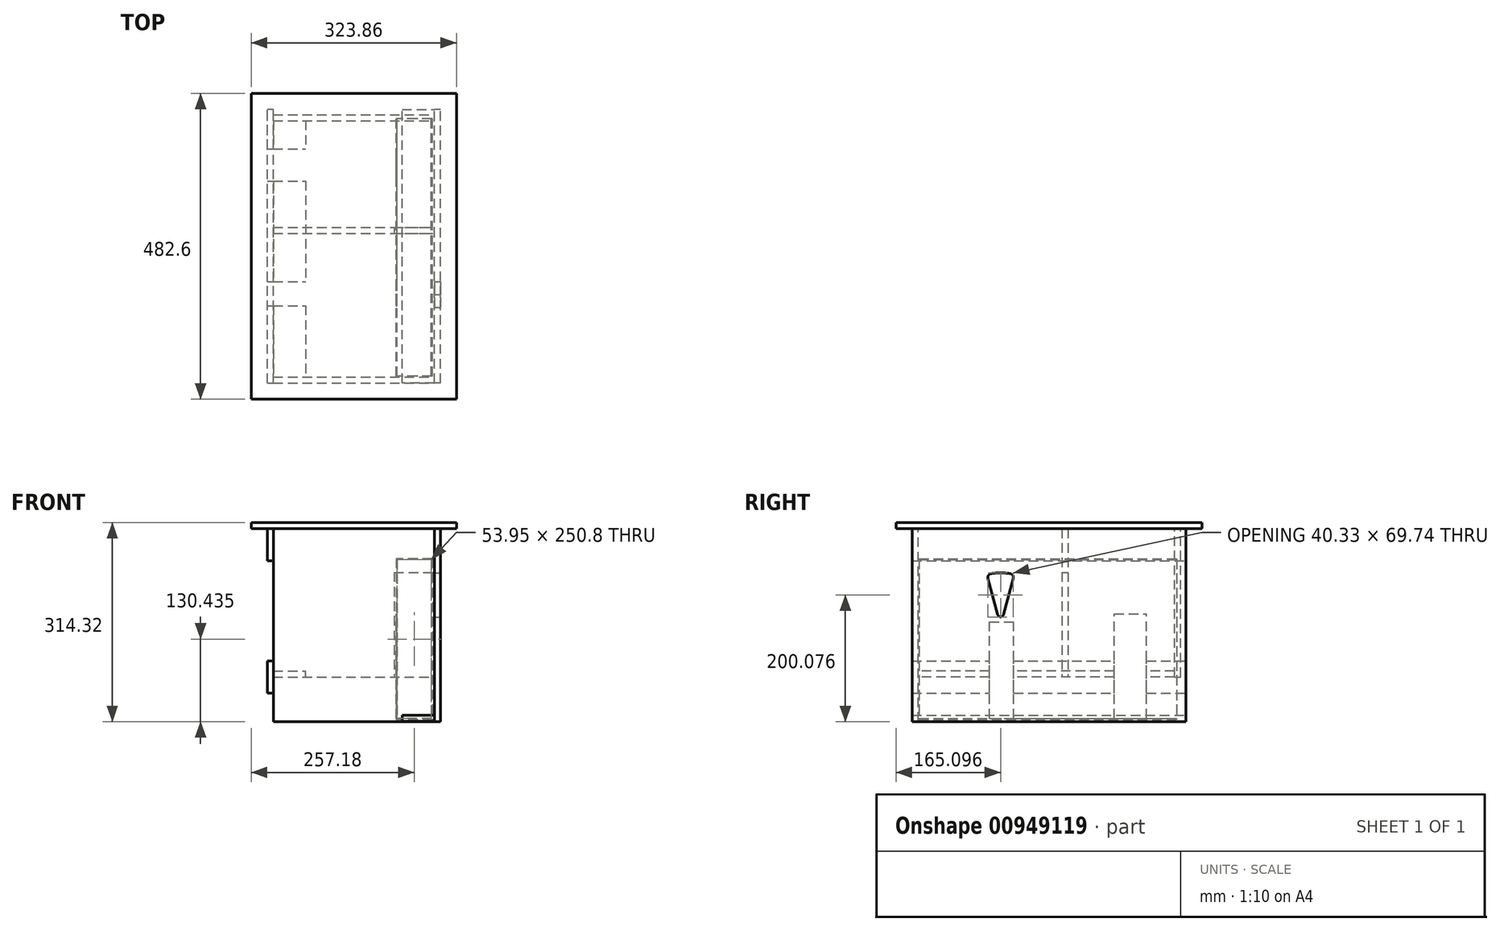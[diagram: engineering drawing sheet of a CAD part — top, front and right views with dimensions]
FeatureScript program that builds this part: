
annotation { "Feature Type Name" : "Feature", "Feature Type Description" : "" }
export const myFeature = defineFeature(function(context is Context, id is Id, definition is map)
    precondition{}
    {
        {
            var Q0;
            Q0=qCreatedBy(makeId("Right.planeOp"),FACE);
            var sketch = newSketch(context, id + "F0", { "sketchPlane" : qUnion([Q0])});
            skLineSegment(sketch, "E0", {"start": v(-148.93, -18.34) * mm, "end": v(130.45, -14.96) * mm});
            skCircle(sketch, "E1", {"center": v(-116.9, 185.56) * mm, "radius": 114.3 * mm});
            skCircle(sketch, "E2", {"center": v(85.94, 209.07) * mm, "radius": 38.1 * mm});
            skCircle(sketch, "E3", {"center": v(142.36, 82.13) * mm, "radius": 9.5 * mm});
            skCircle(sketch, "E4", {"center": v(187.36, 99.59) * mm, "radius": 9.5 * mm});
            skLineSegment(sketch, "E5", {"start": v(-180.7, 129.14) * mm, "end": v(192.06, 129.14) * mm});
            skLineSegment(sketch, "E6", {"start": v(-122.27, 219.14) * mm, "end": v(-101.44, 219.14) * mm});
            skLineSegment(sketch, "E7", {"start": v(-10.1, 98.92) * mm, "end": v(14.75, 107.65) * mm});
            skCircle(sketch, "E8", {"center": v(8.03, 88.17) * mm, "radius": 9.5 * mm});
            skSolve(sketch);
        }
        {
            var Q0;
            Q0=qCreatedBy(makeId("Top.planeOp"),FACE);
            var sketch = newSketch(context, id + "F1", { "sketchPlane" : qUnion([Q0])});
            skLineSegment(sketch, "E9.bottom", {"start": v(-42.95, 107.55) * mm, "end": v(-29.2, 107.55) * mm});
            skLineSegment(sketch, "E9.top", {"start": v(-42.95, 62.2) * mm, "end": v(-29.2, 62.2) * mm});
            skLineSegment(sketch, "E9.left", {"start": v(-42.95, 107.55) * mm, "end": v(-42.95, 62.2) * mm});
            skLineSegment(sketch, "E9.right", {"start": v(-29.2, 107.55) * mm, "end": v(-29.2, 62.2) * mm});
            skLineSegment(sketch, "E10.bottom", {"start": v(-48.66, -104.64) * mm, "end": v(-33.18, -104.64) * mm});
            skLineSegment(sketch, "E10.top", {"start": v(-48.66, -129.08) * mm, "end": v(-33.18, -129.08) * mm});
            skLineSegment(sketch, "E10.left", {"start": v(-48.66, -104.64) * mm, "end": v(-48.66, -129.08) * mm});
            skLineSegment(sketch, "E10.right", {"start": v(-33.18, -104.64) * mm, "end": v(-33.18, -129.08) * mm});
            skLineSegment(sketch, "E11", {"start": v(-46.2, 165.85) * mm, "end": v(-46.2, 7.96) * mm});
            skLineSegment(sketch, "E12", {"start": v(-51.91, -73.7) * mm, "end": v(-51.91, -164.92) * mm});
            skLineSegment(sketch, "E13.bottom", {"start": v(-23.4, -6.61) * mm, "end": v(16.15, -6.61) * mm});
            skLineSegment(sketch, "E13.top", {"start": v(-23.4, -228.46) * mm, "end": v(16.15, -228.46) * mm});
            skLineSegment(sketch, "E13.left", {"start": v(-23.4, -6.61) * mm, "end": v(-23.4, -228.46) * mm});
            skLineSegment(sketch, "E13.right", {"start": v(16.15, -6.61) * mm, "end": v(16.15, -228.46) * mm});
            skLineSegment(sketch, "E14.bottom", {"start": v(-11.19, 125.36) * mm, "end": v(9.67, 125.36) * mm});
            skLineSegment(sketch, "E14.top", {"start": v(-11.19, 44.4) * mm, "end": v(9.67, 44.4) * mm});
            skLineSegment(sketch, "E14.left", {"start": v(-11.19, 125.36) * mm, "end": v(-11.19, 44.4) * mm});
            skLineSegment(sketch, "E14.right", {"start": v(9.67, 125.36) * mm, "end": v(9.67, 44.4) * mm});
            skLineSegment(sketch, "E15.bottom", {"start": v(19.39, 92.98) * mm, "end": v(9.67, 92.98) * mm});
            skLineSegment(sketch, "E15.top", {"start": v(19.39, 75.97) * mm, "end": v(9.67, 75.97) * mm});
            skLineSegment(sketch, "E15.left", {"start": v(19.39, 92.98) * mm, "end": v(19.39, 75.97) * mm});
            skLineSegment(sketch, "E15.right", {"start": v(9.67, 92.98) * mm, "end": v(9.67, 75.97) * mm});
            skLineSegment(sketch, "E16", {"start": v(-21.1, 178.8) * mm, "end": v(-21.1, 106.74) * mm});
            skLineSegment(sketch, "E17.bottom", {"start": v(-26.76, 9.58) * mm, "end": v(18.58, 4.72) * mm});
            skLineSegment(sketch, "E17.top", {"start": v(-29.12, -12.45) * mm, "end": v(16.22, -17.31) * mm});
            skLineSegment(sketch, "E17.left", {"start": v(-26.76, 9.58) * mm, "end": v(-29.12, -12.45) * mm});
            skLineSegment(sketch, "E17.right", {"start": v(18.58, 4.72) * mm, "end": v(16.22, -17.31) * mm});
            skCircle(sketch, "E18", {"center": v(-117.44, -142.64) * mm, "radius": 73.87 * mm});
            skLineSegment(sketch, "E19", {"start": v(0, -116.9) * mm, "end": v(98.98, -116.9) * mm});
            skLineSegment(sketch, "E20", {"start": v(0, 85.94) * mm, "end": v(94.12, 85.94) * mm});
            skSolve(sketch);
        }
        {
            var Q0;
            Q0=qCreatedBy(makeId("Right.planeOp"),FACE);
            var sketch = newSketch(context, id + "F2", { "sketchPlane" : qUnion([Q0])});
            skLineSegment(sketch, "E21", {"start": v(-131.58, 219.14) * mm, "end": v(-90.11, 219.14) * mm});
            skLineSegment(sketch, "E22.0", {"start": v(-256.6, 58.56) * mm, "end": v(175.2, 58.56) * mm});
            skLineSegment(sketch, "E23", {"start": v(-256.6, 363.36) * mm, "end": v(175.2, 363.36) * mm});
            skLineSegment(sketch, "E24", {"start": v(175.2, 363.36) * mm, "end": v(175.2, 58.56) * mm});
            skLineSegment(sketch, "E25", {"start": v(-256.6, 363.36) * mm, "end": v(-256.6, 58.56) * mm});
            skPoint(sketch, "E26.orphan", {"position": v(-180.7, 129.14) * mm});
            skPoint(sketch, "E27.orphan", {"position": v(192.06, 129.14) * mm});
            skCircle(sketch, "E28.0", {"center": v(85.94, 209.07) * mm, "radius": 38.1 * mm, "construction": true});
            skCircle(sketch, "E29.0", {"center": v(-116.9, 185.56) * mm, "radius": 114.3 * mm, "construction": true});
            skLineSegment(sketch, "E30", {"start": v(124.04, 209.07) * mm, "end": v(175.2, 209.07) * mm, "construction": true});
            skLineSegment(sketch, "E31", {"start": v(-231.2, 185.56) * mm, "end": v(-256.6, 185.56) * mm, "construction": true});
            skLineSegment(sketch, "E32", {"start": v(-116.9, 299.86) * mm, "end": v(-116.9, 363.36) * mm, "construction": true});
            skSolve(sketch);
        }
        {
            var Q0;
            Q0 = qSketchRegion(id + "F2", true);
            extrude(context, id + "F3", {"entities" : qUnion([Q0]), "depth" : 41.27 * mm, "offsetDistance" : 25.4 * mm, "hasSecondDirection" : true, "secondDirectionOppositeDirection" : false, "secondDirectionDepth" : 31.75 * mm});
        }
        {
            var Q0;
            Q0=makeQuery(id+"F3.opExtrude","CAP_FACE",FACE,{"disambiguationData":[OSD([sQuery(id+"F2.wireOp",EDGE,"E22.0"),sQuery(id+"F2.wireOp",EDGE,"E23"),sQuery(id+"F2.wireOp",EDGE,"E24"),sQuery(id+"F2.wireOp",EDGE,"E25")])],"isStart":true});
            var sketch = newSketch(context, id + "F4", { "sketchPlane" : qUnion([Q0])});
            skLineSegment(sketch, "E33.bottom", {"start": v(10.68, 363.36) * mm, "end": v(20.2, 363.36) * mm});
            skLineSegment(sketch, "E33.top", {"start": v(10.68, 129.14) * mm, "end": v(20.2, 129.14) * mm});
            skLineSegment(sketch, "E33.left", {"start": v(10.68, 363.36) * mm, "end": v(10.68, 129.14) * mm});
            skLineSegment(sketch, "E33.right", {"start": v(20.2, 363.36) * mm, "end": v(20.2, 129.14) * mm});
            skSolve(sketch);
        }
        {
            var Q0;
            Q0 = qSketchRegion(id + "F4", true);
            extrude(context, id + "F5", {"entities" : qUnion([Q0]), "depth" : 254 * mm, "offsetDistance" : 25.4 * mm});
        }
        {
            var Q0;
            Q0=makeQuery(id+"F5.opExtrude","SWEPT_FACE",FACE,{"disambiguationData":[OSD([sQuery(id+"F4.wireOp",EDGE,"E33.top")])]});
            var sketch = newSketch(context, id + "F6", { "sketchPlane" : qUnion([Q0])});
            skLineSegment(sketch, "E34.bottom", {"start": v(-219.08, 20.2) * mm, "end": v(31.75, 20.2) * mm});
            skLineSegment(sketch, "E34.top", {"start": v(-219.08, 10.68) * mm, "end": v(31.75, 10.68) * mm});
            skLineSegment(sketch, "E34.right", {"start": v(31.75, 20.2) * mm, "end": v(31.75, 10.68) * mm});
            skLineSegment(sketch, "E35", {"start": v(-219.08, 10.68) * mm, "end": v(-219.08, 20.2) * mm});
            skSolve(sketch);
        }
        {
            var Q0;
            Q0=makeQuery(id+"F5.opExtrude","CAP_FACE",FACE,{"disambiguationData":[OSD([sQuery(id+"F4.wireOp",EDGE,"E33.bottom"),sQuery(id+"F4.wireOp",EDGE,"E33.top"),sQuery(id+"F4.wireOp",EDGE,"E33.left"),sQuery(id+"F4.wireOp",EDGE,"E33.right")])],"isStart":true});
            var sketch = newSketch(context, id + "F7", { "sketchPlane" : qUnion([Q0])});
            skLineSegment(sketch, "E36.bottom", {"start": v(-20.2, 294.24) * mm, "end": v(-10.68, 294.24) * mm});
            skLineSegment(sketch, "E36.top", {"start": v(-20.2, 129.14) * mm, "end": v(-10.68, 129.14) * mm});
            skLineSegment(sketch, "E36.left", {"start": v(-20.2, 294.24) * mm, "end": v(-20.2, 129.14) * mm});
            skLineSegment(sketch, "E36.right", {"start": v(-10.68, 294.24) * mm, "end": v(-10.68, 129.14) * mm});
            skSolve(sketch);
        }
        {
            var Q0;
            Q0 = qSketchRegion(id + "F7", true);
            extrude(context, id + "F8", {"entities" : qUnion([Q0]), "operationType" : NewBodyOperationType.REMOVE, "oppositeDirection" : true, "depth" : 63.5 * mm, "offsetDistance" : 25.4 * mm});
        }
        {
            var Q0;
            Q0=makeQuery(id+"F5.opExtrude","CAP_FACE",FACE,{"disambiguationData":[OSD([sQuery(id+"F4.wireOp",EDGE,"E33.bottom"),sQuery(id+"F4.wireOp",EDGE,"E33.top"),sQuery(id+"F4.wireOp",EDGE,"E33.left"),sQuery(id+"F4.wireOp",EDGE,"E33.right")])],"isStart":true});
            var sketch = newSketch(context, id + "F9", { "sketchPlane" : qUnion([Q0])});
            skLineSegment(sketch, "E37.bottom", {"start": v(157.6, 129.14) * mm, "end": v(167.12, 129.14) * mm});
            skLineSegment(sketch, "E37.top", {"start": v(157.6, 363.36) * mm, "end": v(167.12, 363.36) * mm});
            skLineSegment(sketch, "E37.left", {"start": v(157.6, 129.14) * mm, "end": v(157.6, 363.36) * mm});
            skLineSegment(sketch, "E37.right", {"start": v(167.12, 129.14) * mm, "end": v(167.12, 363.36) * mm});
            skSolve(sketch);
        }
        {
            var Q0;
            Q0 = qSketchRegion(id + "F9", true);
            var Q1;
            Q1=makeQuery(id+"F5.opExtrude","CAP_FACE",FACE,{"disambiguationData":[OSD([sQuery(id+"F4.wireOp",EDGE,"E33.bottom"),sQuery(id+"F4.wireOp",EDGE,"E33.top"),sQuery(id+"F4.wireOp",EDGE,"E33.left"),sQuery(id+"F4.wireOp",EDGE,"E33.right")])],"isStart":false});
            extrude(context, id + "F10", {"entities" : qUnion([Q0]), "endBound" : BoundingType.UP_TO_SURFACE, "oppositeDirection" : true, "depth" : 25.4 * mm, "endBoundEntityFace" : qUnion([Q1]), "offsetDistance" : 25.4 * mm});
        }
        {
            var Q0;
            Q0=makeQuery(id+"F5.opExtrude","CAP_FACE",FACE,{"disambiguationData":[OSD([sQuery(id+"F4.wireOp",EDGE,"E33.bottom"),sQuery(id+"F4.wireOp",EDGE,"E33.top"),sQuery(id+"F4.wireOp",EDGE,"E33.left"),sQuery(id+"F4.wireOp",EDGE,"E33.right")])],"isStart":true});
            var sketch = newSketch(context, id + "F11", { "sketchPlane" : qUnion([Q0])});
            skLineSegment(sketch, "E38.bottom", {"start": v(-256.6, 58.56) * mm, "end": v(-247.07, 58.56) * mm});
            skLineSegment(sketch, "E38.top", {"start": v(-256.6, 363.36) * mm, "end": v(-247.07, 363.36) * mm});
            skLineSegment(sketch, "E38.left", {"start": v(-256.6, 58.56) * mm, "end": v(-256.6, 363.36) * mm});
            skLineSegment(sketch, "E38.right", {"start": v(-247.07, 58.56) * mm, "end": v(-247.07, 363.36) * mm});
            skSolve(sketch);
        }
        {
            var Q0;
            Q0 = qSketchRegion(id + "F11", true);
            var Q1;
            Q1=makeQuery(id+"F5.opExtrude","CAP_FACE",FACE,{"disambiguationData":[OSD([sQuery(id+"F4.wireOp",EDGE,"E33.bottom"),sQuery(id+"F4.wireOp",EDGE,"E33.top"),sQuery(id+"F4.wireOp",EDGE,"E33.left"),sQuery(id+"F4.wireOp",EDGE,"E33.right")])],"isStart":false});
            extrude(context, id + "F12", {"entities" : qUnion([Q0]), "endBound" : BoundingType.UP_TO_SURFACE, "oppositeDirection" : true, "depth" : 25.4 * mm, "endBoundEntityFace" : qUnion([Q1]), "offsetDistance" : 25.4 * mm});
        }
        {
            var Q0;
            Q0=makeQuery(id+"F3.opExtrude","CAP_FACE",FACE,{"disambiguationData":[OSD([sQuery(id+"F2.wireOp",EDGE,"E22.0"),sQuery(id+"F2.wireOp",EDGE,"E23"),sQuery(id+"F2.wireOp",EDGE,"E24"),sQuery(id+"F2.wireOp",EDGE,"E25")])],"isStart":false});
            var sketch = newSketch(context, id + "F13", { "sketchPlane" : qUnion([Q0])});
            skCircle(sketch, "E39", {"center": v(-116.9, 185.56) * mm, "radius": 107.95 * mm});
            skCircle(sketch, "E40", {"center": v(-116.9, 185.56) * mm, "radius": 38.1 * mm});
            skLineSegment(sketch, "E41", {"start": v(-116.9, 185.56) * mm, "end": v(-144.83, 289.83) * mm, "construction": true});
            skLineSegment(sketch, "E42", {"start": v(-144.83, 289.83) * mm, "end": v(-88.95, 289.83) * mm, "construction": true});
            skLineSegment(sketch, "E43", {"start": v(-88.95, 289.83) * mm, "end": v(-116.9, 185.56) * mm, "construction": true});
            skLineSegment(sketch, "E44", {"start": v(-116.9, 185.56) * mm, "end": v(-116.9, 289.83) * mm, "construction": true});
            skPoint(sketch, "E44.endSnap0", {"position": v(-116.9, 289.83) * mm});
            skLineSegment(sketch, "E45.0", {"start": v(-120.48, 223.49) * mm, "end": v(-138.65, 291.3) * mm});
            skLineSegment(sketch, "E46.0", {"start": v(-95.14, 291.3) * mm, "end": v(-113.3, 223.49) * mm});
            skSolve(sketch);
        }
        {
            var Q0;
            {var subQ0=sQuery(id+"F13.wireOp",EDGE,"E45.0");Q0=makeQuery(id+"F13.imprint","IMPRINT",FACE,{"disambiguationData":[TD([[makeQuery(id+"F13.imprint","IMPRINT",EDGE,{"derivedFrom":subQ0}),-1.0]])]});}
            extrude(context, id + "F14", {"entities" : qUnion([Q0]), "operationType" : NewBodyOperationType.REMOVE, "endBound" : BoundingType.THROUGH_ALL, "oppositeDirection" : true, "depth" : 25.4 * mm, "offsetDistance" : 25.4 * mm});
        }
        {
            var Q0;
            Q0=makeQuery(id+"F14.boolean.opBoolean","COPY",EDGE,{"derivedFrom":makeQuery(id+"F14.opExtrude","SWEPT_EDGE",EDGE,{"disambiguationData":[OSD([sQuery(id+"F13.wireOp",EDGE,"E39"),sQuery(id+"F13.wireOp",EDGE,"E46.0")])]})});
            var Q1;
            Q1=makeQuery(id+"F14.boolean.opBoolean","COPY",EDGE,{"derivedFrom":makeQuery(id+"F14.opExtrude","SWEPT_EDGE",EDGE,{"disambiguationData":[OSD([sQuery(id+"F13.wireOp",EDGE,"E39"),sQuery(id+"F13.wireOp",EDGE,"E45.0")])]})});
            var Q2;
            Q2=makeQuery(id+"F14.boolean.opBoolean","COPY",EDGE,{"derivedFrom":makeQuery(id+"F14.opExtrude","SWEPT_EDGE",EDGE,{"disambiguationData":[OSD([sQuery(id+"F13.wireOp",EDGE,"E40"),sQuery(id+"F13.wireOp",EDGE,"E45.0")])]})});
            var Q3;
            Q3=makeQuery(id+"F14.boolean.opBoolean","COPY",EDGE,{"derivedFrom":makeQuery(id+"F14.opExtrude","SWEPT_EDGE",EDGE,{"disambiguationData":[OSD([sQuery(id+"F13.wireOp",EDGE,"E40"),sQuery(id+"F13.wireOp",EDGE,"E46.0")])]})});
            fillet(context, id + "F15", {"entities" : qUnion([Q0, Q1, Q2, Q3]), "radius" : 6.35 * mm, "tangentPropagation" : true, "allowEdgeOverflow" : false});
        }
        {
            var Q0;
            Q0=makeQuery(id+"F3.opExtrude","SWEPT_FACE",FACE,{"disambiguationData":[OSD([sQuery(id+"F2.wireOp",EDGE,"E24")])]});
            var sketch = newSketch(context, id + "F16", { "sketchPlane" : qUnion([Q0])});
            skLineSegment(sketch, "E47.bottom", {"start": v(222.25, 154.54) * mm, "end": v(231.78, 154.54) * mm});
            skLineSegment(sketch, "E47.top", {"start": v(222.25, 103.74) * mm, "end": v(231.78, 103.74) * mm});
            skLineSegment(sketch, "E47.left", {"start": v(222.25, 154.54) * mm, "end": v(222.25, 103.74) * mm});
            skLineSegment(sketch, "E47.right", {"start": v(231.78, 154.54) * mm, "end": v(231.78, 103.74) * mm});
            skSolve(sketch);
        }
        {
            var Q0;
            Q0 = qSketchRegion(id + "F16", true);
            var Q1;
            Q1=makeQuery(id+"F3.opExtrude","SWEPT_FACE",FACE,{"disambiguationData":[OSD([sQuery(id+"F2.wireOp",EDGE,"E25")])]});
            extrude(context, id + "F17", {"entities" : qUnion([Q0]), "endBound" : BoundingType.UP_TO_SURFACE, "oppositeDirection" : true, "depth" : 25.4 * mm, "endBoundEntityFace" : qUnion([Q1]), "offsetDistance" : 25.4 * mm});
        }
        {
            var Q0;
            Q0=makeQuery(id+"F12.opExtrude","SWEPT_FACE",FACE,{"disambiguationData":[OSD([sQuery(id+"F11.wireOp",EDGE,"E38.right")])]});
            var sketch = newSketch(context, id + "F18", { "sketchPlane" : qUnion([Q0])});
            skLineSegment(sketch, "E48.bottom", {"start": v(222.25, 129.14) * mm, "end": v(171.45, 129.14) * mm});
            skLineSegment(sketch, "E48.top", {"start": v(222.25, 138.67) * mm, "end": v(171.45, 138.67) * mm});
            skLineSegment(sketch, "E48.left", {"start": v(222.25, 129.14) * mm, "end": v(222.25, 138.67) * mm});
            skLineSegment(sketch, "E48.right", {"start": v(171.45, 129.14) * mm, "end": v(171.45, 138.67) * mm});
            skSolve(sketch);
        }
        {
            var Q0;
            Q0 = qSketchRegion(id + "F18", true);
            var Q1;
            Q1=makeQuery(id+"F10.opExtrude","SWEPT_FACE",FACE,{"disambiguationData":[OSD([sQuery(id+"F9.wireOp",EDGE,"E37.left")])]});
            extrude(context, id + "F19", {"entities" : qUnion([Q0]), "endBound" : BoundingType.UP_TO_SURFACE, "depth" : 25.4 * mm, "endBoundEntityFace" : qUnion([Q1]), "offsetDistance" : 25.4 * mm});
        }
        {
            var Q0;
            Q0=makeQuery(id+"F3.opExtrude","SWEPT_FACE",FACE,{"disambiguationData":[OSD([sQuery(id+"F2.wireOp",EDGE,"E23")])]});
            var sketch = newSketch(context, id + "F20", { "sketchPlane" : qUnion([Q0])});
            skLineSegment(sketch, "E49.bottom", {"start": v(66.68, -282) * mm, "end": v(-257.17, -282) * mm});
            skLineSegment(sketch, "E49.top", {"start": v(66.67, 200.6) * mm, "end": v(-257.18, 200.6) * mm});
            skLineSegment(sketch, "E49.left", {"start": v(66.68, -282) * mm, "end": v(66.68, 200.6) * mm});
            skLineSegment(sketch, "E49.right", {"start": v(-257.17, -282) * mm, "end": v(-257.18, 200.6) * mm});
            skSolve(sketch);
        }
        {
            var Q0;
            Q0 = qSketchRegion(id + "F20", true);
            extrude(context, id + "F21", {"entities" : qUnion([Q0]), "depth" : 9.52 * mm, "offsetDistance" : 25.4 * mm});
        }
        {
            var Q0;
            Q0=makeQuery(id+"F17.opExtrude","SWEPT_BODY",BODY,{"disambiguationData":[OSD([sQuery(id+"F16.wireOp",EDGE,"E47.bottom"),sQuery(id+"F16.wireOp",EDGE,"E47.top"),sQuery(id+"F16.wireOp",EDGE,"E47.left"),sQuery(id+"F16.wireOp",EDGE,"E47.right")])]});
            transform(context, id + "F22", {"entities" : qUnion([Q0]), "transformType" : TransformType.TRANSLATION_3D, "dx" : 0 * mm, "dy" : 0 * mm, "dz" : 208.9 * mm, "makeCopy" : true});
        }
        {
            var Q0;
            Q0=makeQuery(id+"F17.opExtrude","SWEPT_BODY",BODY,{"disambiguationData":[OSD([sQuery(id+"F16.wireOp",EDGE,"E47.bottom"),sQuery(id+"F16.wireOp",EDGE,"E47.top"),sQuery(id+"F16.wireOp",EDGE,"E47.left"),sQuery(id+"F16.wireOp",EDGE,"E47.right")])]});
            transform(context, id + "F23", {"entities" : qUnion([Q0]), "transformType" : TransformType.TRANSLATION_3D, "dx" : 254 * mm, "dy" : 0 * mm, "dz" : -34.92 * mm, "makeCopy" : true});
        }
        {
            var Q0;
            Q0=makeQuery(id+"F23.opPattern","COPY",BODY,{"derivedFrom":makeQuery(id+"F17.opExtrude","SWEPT_BODY",BODY,{"disambiguationData":[OSD([sQuery(id+"F16.wireOp",EDGE,"E47.bottom"),sQuery(id+"F16.wireOp",EDGE,"E47.top"),sQuery(id+"F16.wireOp",EDGE,"E47.left"),sQuery(id+"F16.wireOp",EDGE,"E47.right")])]}),"instanceName":"1"});
            var Q1;
            Q1=makeQuery(id+"F23.opPattern","COPY",EDGE,{"derivedFrom":makeQuery(id+"F17.opExtrude","SWEPT_EDGE",EDGE,{"disambiguationData":[OSD([sQuery(id+"F16.wireOp",EDGE,"E47.top"),sQuery(id+"F16.wireOp",EDGE,"E47.left")])]}),"instanceName":"1"});
            transform(context, id + "F24", {"entities" : qUnion([Q0]), "transformType" : TransformType.ROTATION, "transformAxis" : qUnion([Q1]), "angle" : 90 * degree, "oppositeDirection" : true, "makeCopy" : false});
        }
        {
            var Q0;
            Q0=qCreatedBy(makeId("Right.planeOp"),FACE);
            var sketch = newSketch(context, id + "F25", { "sketchPlane" : qUnion([Q0])});
            skLineSegment(sketch, "E50.bottom", {"start": v(-245.55, 316) * mm, "end": v(160.85, 316) * mm});
            skLineSegment(sketch, "E50.top", {"start": v(-245.55, 62) * mm, "end": v(160.85, 62) * mm});
            skLineSegment(sketch, "E50.left", {"start": v(-245.55, 316) * mm, "end": v(-245.55, 62) * mm});
            skLineSegment(sketch, "E50.right", {"start": v(160.85, 316) * mm, "end": v(160.85, 62) * mm});
            skSolve(sketch);
        }
        {
            var Q0;
            Q0 = qSketchRegion(id + "F25", true);
            extrude(context, id + "F26", {"entities" : qUnion([Q0]), "endBound" : BoundingType.SYMMETRIC, "depth" : 57.15 * mm, "offsetDistance" : 25.4 * mm});
        }
        {
            var Q0;
            Q0=makeQuery(id+"F26.opExtrude","SWEPT_FACE",FACE,{"disambiguationData":[OSD([sQuery(id+"F25.wireOp",EDGE,"E50.left")])]});
            var Q1;
            Q1=makeQuery(id+"F26.opExtrude","SWEPT_FACE",FACE,{"disambiguationData":[OSD([sQuery(id+"F25.wireOp",EDGE,"E50.right")])]});
            shell(context, id + "F27", {"entities" : qUnion([Q0, Q1]), "thickness" : 1.6 * mm});
        }
        {
            var Q0;
            {var subQ0=sQuery(id+"F25.wireOp",EDGE,"E50.right");var subQ1=sQuery(id+"F25.wireOp",EDGE,"E50.left");var subQ2=sQuery(id+"F25.wireOp",EDGE,"E50.top");var subQ3=sQuery(id+"F25.wireOp",EDGE,"E50.bottom");Q0=makeQuery(id+"F27.opShell","OFFSET_FACE",FACE,{"disambiguationData":[OSD([subQ3,subQ2,subQ1,subQ0]),TDD([makeQuery(id+"F26.opExtrude","CAP_FACE",FACE,{"disambiguationData":[OSD([subQ3,subQ2,subQ1,subQ0])],"isStart":true})])]});}
            var sketch = newSketch(context, id + "F28", { "sketchPlane" : qUnion([Q0])});
            skLineSegment(sketch, "E51.bottom", {"start": v(-134.43, 63.6) * mm, "end": v(-96.33, 63.6) * mm});
            skLineSegment(sketch, "E51.top", {"start": v(-134.43, 216) * mm, "end": v(-96.33, 216) * mm});
            skLineSegment(sketch, "E51.left", {"start": v(-134.43, 63.6) * mm, "end": v(-134.43, 216) * mm});
            skLineSegment(sketch, "E51.right", {"start": v(-96.33, 63.6) * mm, "end": v(-96.33, 216) * mm});
            skLineSegment(sketch, "E52.bottom", {"start": v(62.42, 63.6) * mm, "end": v(113.22, 63.6) * mm});
            skLineSegment(sketch, "E52.top", {"start": v(62.42, 228.7) * mm, "end": v(113.22, 228.7) * mm});
            skLineSegment(sketch, "E52.left", {"start": v(62.42, 63.6) * mm, "end": v(62.42, 228.7) * mm});
            skLineSegment(sketch, "E52.right", {"start": v(113.22, 63.6) * mm, "end": v(113.22, 228.7) * mm});
            skPoint(sketch, "E53", {"position": v(-115.38, 63.6) * mm});
            skPoint(sketch, "E54", {"position": v(87.82, 63.6) * mm});
            skSolve(sketch);
        }
        {
            var Q0;
            Q0 = qSketchRegion(id + "F28", true);
            extrude(context, id + "F29", {"entities" : qUnion([Q0]), "operationType" : NewBodyOperationType.REMOVE, "endBound" : BoundingType.THROUGH_ALL, "oppositeDirection" : true, "depth" : 25.4 * mm, "offsetDistance" : 25.4 * mm});
        }
    });
